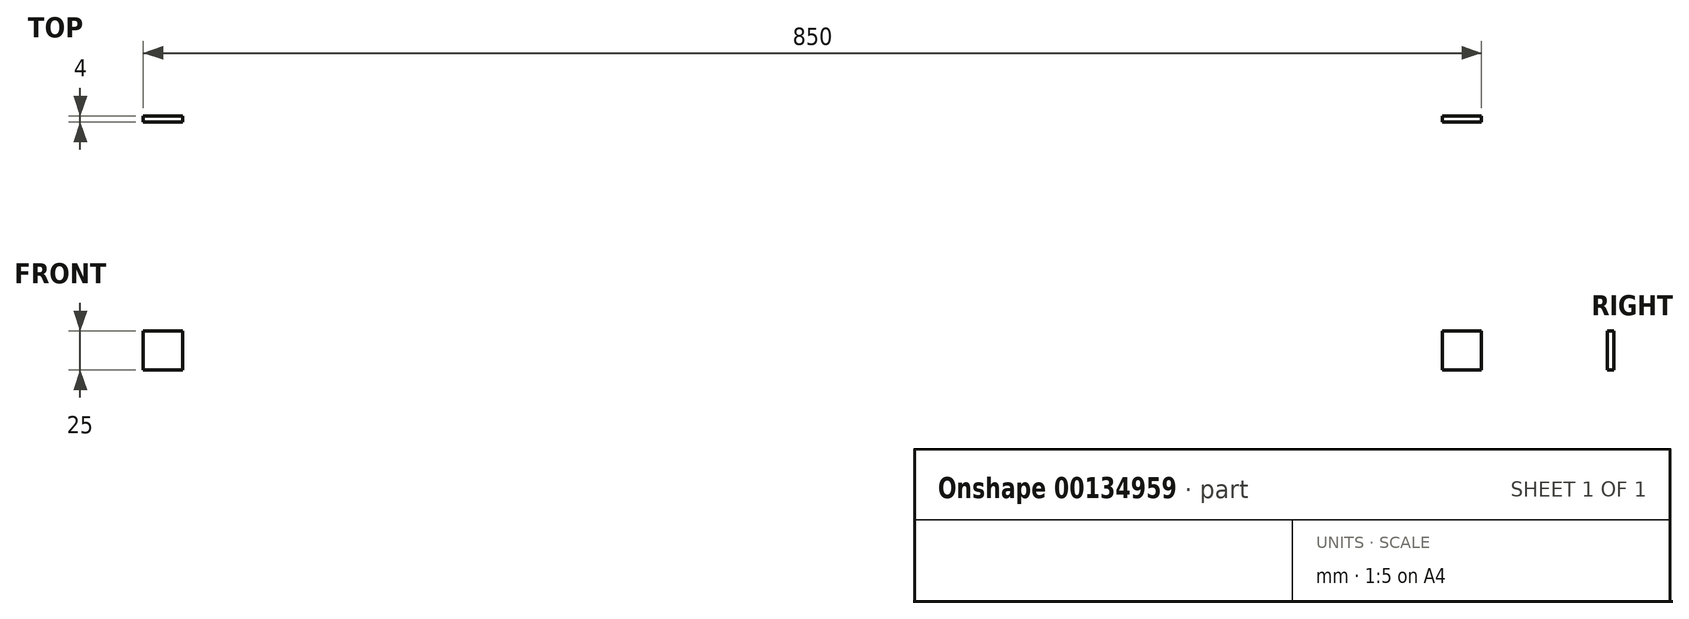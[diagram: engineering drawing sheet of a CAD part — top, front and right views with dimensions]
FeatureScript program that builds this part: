
annotation { "Feature Type Name" : "Feature", "Feature Type Description" : "" }
export const myFeature = defineFeature(function(context is Context, id is Id, definition is map)
    precondition{}
    {
        {
            var Q0;
            Q0=qCreatedBy(makeId("Front.planeOp"),FACE);
            var sketch = newSketch(context, id + "F0", { "sketchPlane" : qUnion([Q0])});
            skLineSegment(sketch, "E0.bottom", {"start": v(0, 0) * mm, "end": v(850, 0) * mm});
            skLineSegment(sketch, "E0.top", {"start": v(0, 507) * mm, "end": v(850, 507) * mm});
            skLineSegment(sketch, "E0.left", {"start": v(0, 0) * mm, "end": v(0, 507) * mm});
            skLineSegment(sketch, "E0.right", {"start": v(850, 0) * mm, "end": v(850, 507) * mm});
            skLineSegment(sketch, "E1.bottom", {"start": v(0, 507) * mm, "end": v(25, 507) * mm});
            skLineSegment(sketch, "E1.top", {"start": v(0, 482) * mm, "end": v(25, 482) * mm});
            skLineSegment(sketch, "E1.left", {"start": v(0, 507) * mm, "end": v(0, 482) * mm});
            skLineSegment(sketch, "E1.right", {"start": v(25, 507) * mm, "end": v(25, 482) * mm});
            skLineSegment(sketch, "E2.bottom", {"start": v(850, 507) * mm, "end": v(825, 507) * mm});
            skLineSegment(sketch, "E2.top", {"start": v(850, 482) * mm, "end": v(825, 482) * mm});
            skLineSegment(sketch, "E2.left", {"start": v(850, 507) * mm, "end": v(850, 482) * mm});
            skLineSegment(sketch, "E2.right", {"start": v(825, 507) * mm, "end": v(825, 482) * mm});
            skLineSegment(sketch, "E3.bottom", {"start": v(850, 0) * mm, "end": v(825, 0) * mm});
            skLineSegment(sketch, "E3.top", {"start": v(850, 25) * mm, "end": v(825, 25) * mm});
            skLineSegment(sketch, "E3.left", {"start": v(850, 0) * mm, "end": v(850, 25) * mm});
            skLineSegment(sketch, "E3.right", {"start": v(825, 0) * mm, "end": v(825, 25) * mm});
            skLineSegment(sketch, "E4.bottom", {"start": v(0, 0) * mm, "end": v(25, 0) * mm});
            skLineSegment(sketch, "E4.top", {"start": v(0, 25) * mm, "end": v(25, 25) * mm});
            skLineSegment(sketch, "E4.left", {"start": v(0, 0) * mm, "end": v(0, 25) * mm});
            skLineSegment(sketch, "E4.right", {"start": v(25, 0) * mm, "end": v(25, 25) * mm});
            skSolve(sketch);
        }
        {
            var Q0;
            Q0=makeQuery(id+"F0.imprint","IMPRINT",FACE,{"disambiguationData":[TD([[makeQuery(id+"F0.imprint","IMPRINT",EDGE,{"derivedFrom":sQuery(id+"F0.wireOp",EDGE,"E0.bottom")}),1.0]])]});
            extrude(context, id + "F1", {"entities" : qUnion([Q0]), "depth" : 4 * mm});
        }
    });
